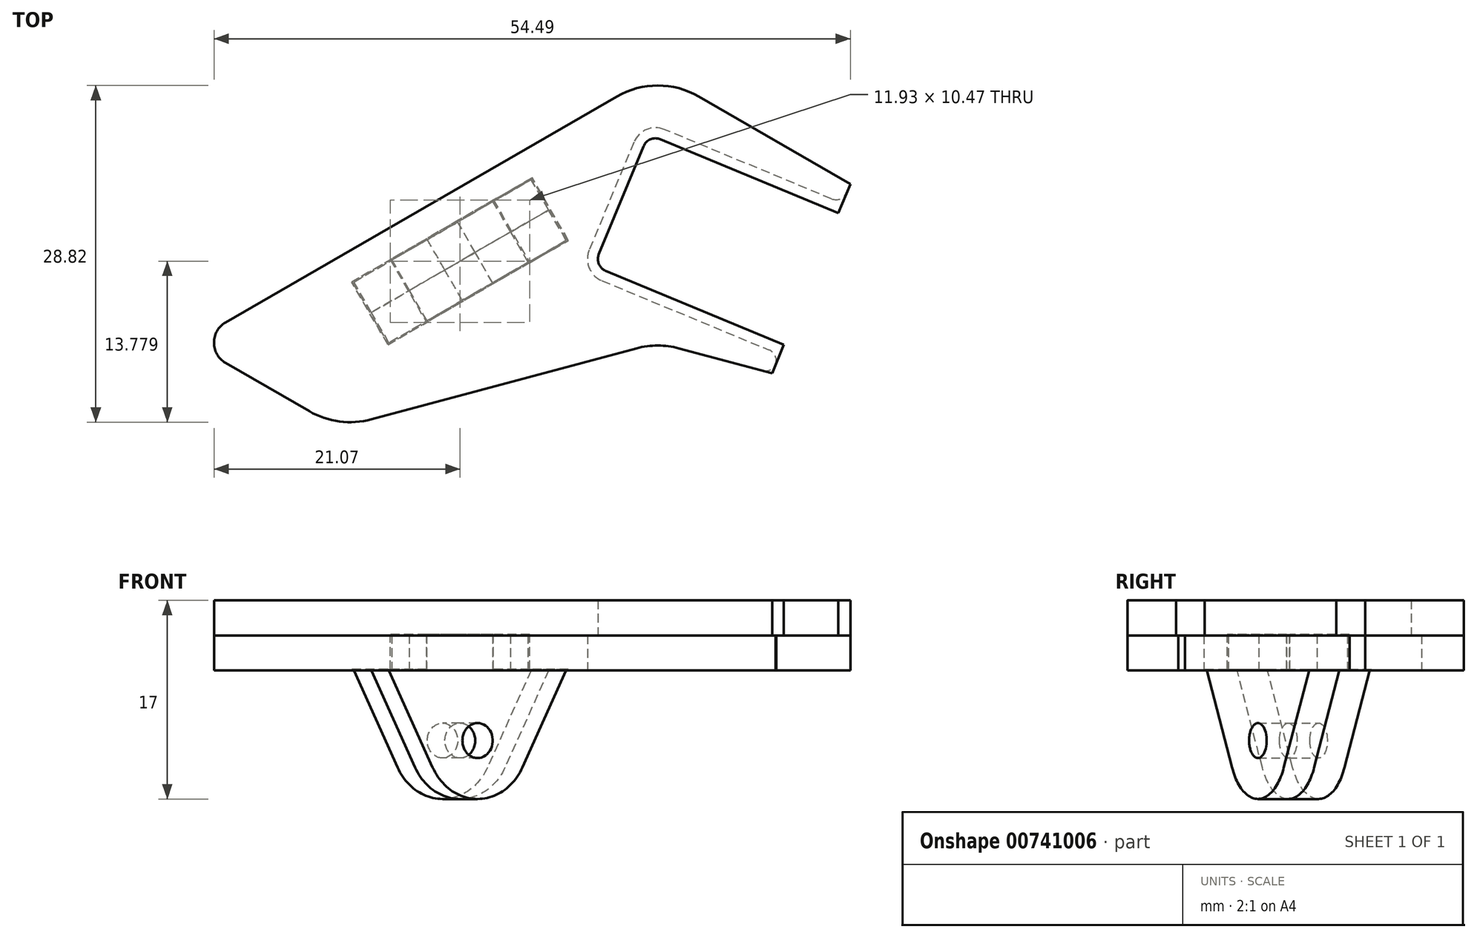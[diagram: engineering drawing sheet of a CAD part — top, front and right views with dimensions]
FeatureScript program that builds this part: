
annotation { "Feature Type Name" : "Feature", "Feature Type Description" : "" }
export const myFeature = defineFeature(function(context is Context, id is Id, definition is map)
    precondition{}
    {
        {
            var Q0;
            Q0=qCreatedBy(makeId("Top.planeOp"),FACE);
            var sketch = newSketch(context, id + "F0", { "sketchPlane" : qUnion([Q0])});
            skLineSegment(sketch, "E0", {"start": v(-37, 1.73) * mm, "end": v(-3.5, 21.07) * mm});
            skLineSegment(sketch, "E1", {"start": v(40, 0) * mm, "end": v(21.73, 10.55) * mm, "construction": true});
            skLineSegment(sketch, "E2", {"start": v(-1.81, -0.49) * mm, "end": v(-24.52, -6.57) * mm});
            skLineSegment(sketch, "E3", {"start": v(0, 0) * mm, "end": v(0, 23.1) * mm, "construction": true});
            skLineSegment(sketch, "E4", {"start": v(40, 0) * mm, "end": v(27.32, -7.32) * mm, "construction": true});
            skLineSegment(sketch, "E5", {"start": v(-29.83, -5.87) * mm, "end": v(-40, 0) * mm});
            skLineSegment(sketch, "E6", {"start": v(27.32, -7.32) * mm, "end": v(0, -23.1) * mm, "construction": true});
            skLineSegment(sketch, "E7", {"start": v(0, -23.1) * mm, "end": v(-37, -1.73) * mm, "construction": true});
            skLineSegment(sketch, "E8", {"start": v(13.99, -0.3) * mm, "end": v(17.82, 8.93) * mm});
            skLineSegment(sketch, "E9", {"start": v(16.73, 11.54) * mm, "end": v(0.57, 18.24) * mm});
            skLineSegment(sketch, "E10", {"start": v(-2.05, 17.16) * mm, "end": v(-5.87, 7.92) * mm});
            skLineSegment(sketch, "E11", {"start": v(-4.8, 5.3) * mm, "end": v(11.38, -1.4) * mm});
            skPoint(sketch, "E12.visualSharp", {"position": v(-6.64, 6.07) * mm});
            skArc(sketch, "E12.filletArc", {"start": v(-5.87, 7.92) * mm, "mid": v(-5.87, 6.39) * mm, "end": v(-4.8, 5.3) * mm});
            skPoint(sketch, "E13.visualSharp", {"position": v(-1.28, 19) * mm});
            skArc(sketch, "E13.filletArc", {"start": v(0.57, 18.24) * mm, "mid": v(-0.96, 18.24) * mm, "end": v(-2.05, 17.16) * mm});
            skPoint(sketch, "E14.visualSharp", {"position": v(18.58, 10.78) * mm});
            skArc(sketch, "E14.filletArc", {"start": v(17.82, 8.93) * mm, "mid": v(17.82, 10.46) * mm, "end": v(16.73, 11.54) * mm});
            skPoint(sketch, "E15.visualSharp", {"position": v(13.22, -2.16) * mm});
            skArc(sketch, "E15.filletArc", {"start": v(11.38, -1.4) * mm, "mid": v(12.9, -1.4) * mm, "end": v(13.99, -0.3) * mm});
            skLineSegment(sketch, "E16", {"start": v(16.64, -1.76) * mm, "end": v(20.73, 8.12) * mm});
            skLineSegment(sketch, "E17", {"start": v(15.63, -4.19) * mm, "end": v(27.32, -7.32) * mm, "construction": true});
            skLineSegment(sketch, "E18", {"start": v(13.09, -3.5) * mm, "end": v(1.81, -0.49) * mm});
            skLineSegment(sketch, "E19", {"start": v(3.5, 21.07) * mm, "end": v(19.45, 11.86) * mm});
            skPoint(sketch, "E20.visualSharp", {"position": v(15.63, -4.19) * mm});
            skArc(sketch, "E20.filletArc", {"start": v(13.09, -3.5) * mm, "mid": v(15.2, -3.3) * mm, "end": v(16.64, -1.76) * mm});
            skPoint(sketch, "E21.visualSharp", {"position": v(21.73, 10.55) * mm});
            skArc(sketch, "E21.filletArc", {"start": v(20.73, 8.12) * mm, "mid": v(20.8, 10.23) * mm, "end": v(19.45, 11.86) * mm});
            skPoint(sketch, "E22.visualSharp", {"position": v(0, 0) * mm});
            skArc(sketch, "E22.filletArc", {"start": v(1.81, -0.49) * mm, "mid": v(0, -0.25) * mm, "end": v(-1.81, -0.49) * mm});
            skPoint(sketch, "E23.visualSharp", {"position": v(-27.32, -7.32) * mm});
            skArc(sketch, "E23.filletArc", {"start": v(-29.83, -5.87) * mm, "mid": v(-27.25, -6.75) * mm, "end": v(-24.52, -6.57) * mm});
            skPoint(sketch, "E24.visualSharp", {"position": v(0, 23.1) * mm});
            skArc(sketch, "E24.filletArc", {"start": v(3.5, 21.07) * mm, "mid": v(0, 22.01) * mm, "end": v(-3.5, 21.07) * mm});
            skPoint(sketch, "E25.visualSharp", {"position": v(-40, 0) * mm});
            skArc(sketch, "E25.filletArc", {"start": v(-37, 1.73) * mm, "mid": v(-38, 0) * mm, "end": v(-37, -1.73) * mm});
            skSolve(sketch);
        }
        {
            var Q0;
            Q0=makeQuery(id+"F0.imprint","IMPRINT",FACE,{"disambiguationData":[TD([[makeQuery(id+"F0.imprint","IMPRINT",EDGE,{"derivedFrom":sQuery(id+"F0.wireOp",EDGE,"E0")}),-1.0]])]});
            extrude(context, id + "F1", {"entities" : qUnion([Q0]), "depth" : 3 * mm, "offsetDistance" : 25 * mm});
        }
        {
            var Q0;
            Q0=makeQuery(id+"F1.opExtrude","CAP_FACE",FACE,{"disambiguationData":[OSD([sQuery(id+"F0.wireOp",EDGE,"E0"),sQuery(id+"F0.wireOp",EDGE,"E2"),sQuery(id+"F0.wireOp",EDGE,"E5"),sQuery(id+"F0.wireOp",EDGE,"E8"),sQuery(id+"F0.wireOp",EDGE,"E9"),sQuery(id+"F0.wireOp",EDGE,"E10"),sQuery(id+"F0.wireOp",EDGE,"E11"),sQuery(id+"F0.wireOp",EDGE,"E12.filletArc"),sQuery(id+"F0.wireOp",EDGE,"E13.filletArc"),sQuery(id+"F0.wireOp",EDGE,"E14.filletArc"),sQuery(id+"F0.wireOp",EDGE,"E15.filletArc"),sQuery(id+"F0.wireOp",EDGE,"E16"),sQuery(id+"F0.wireOp",EDGE,"E18"),sQuery(id+"F0.wireOp",EDGE,"E19"),sQuery(id+"F0.wireOp",EDGE,"E20.filletArc"),sQuery(id+"F0.wireOp",EDGE,"E21.filletArc"),sQuery(id+"F0.wireOp",EDGE,"E22.filletArc"),sQuery(id+"F0.wireOp",EDGE,"E23.filletArc"),sQuery(id+"F0.wireOp",EDGE,"E24.filletArc"),sQuery(id+"F0.wireOp",EDGE,"E25.filletArc")])],"isStart":false});
            var sketch = newSketch(context, id + "F2", { "sketchPlane" : qUnion([Q0])});
            skArc(sketch, "E26.0", {"start": v(-5.04, 7.58) * mm, "mid": v(-5.04, 6.73) * mm, "end": v(-4.45, 6.14) * mm});
            skLineSegment(sketch, "E26.1", {"start": v(-1.22, 16.81) * mm, "end": v(-5.04, 7.58) * mm});
            skLineSegment(sketch, "E26.2", {"start": v(-4.45, 6.14) * mm, "end": v(11.72, -0.56) * mm});
            skArc(sketch, "E26.3", {"start": v(0.22, 17.4) * mm, "mid": v(-0.62, 17.4) * mm, "end": v(-1.22, 16.81) * mm});
            skArc(sketch, "E26.4", {"start": v(11.72, -0.56) * mm, "mid": v(12.56, -0.56) * mm, "end": v(13.16, 0.04) * mm});
            skLineSegment(sketch, "E26.5", {"start": v(13.16, 0.04) * mm, "end": v(16.98, 9.28) * mm});
            skArc(sketch, "E26.6", {"start": v(16.98, 9.28) * mm, "mid": v(16.98, 10.12) * mm, "end": v(16.39, 10.71) * mm});
            skLineSegment(sketch, "E26.7", {"start": v(16.39, 10.71) * mm, "end": v(0.22, 17.4) * mm});
            skLineSegment(sketch, "E27.0", {"start": v(13.09, -3.5) * mm, "end": v(1.81, -0.49) * mm});
            skArc(sketch, "E28.0", {"start": v(13.09, -3.5) * mm, "mid": v(15.2, -3.3) * mm, "end": v(16.64, -1.76) * mm});
            skLineSegment(sketch, "E29.0", {"start": v(16.64, -1.76) * mm, "end": v(20.73, 8.12) * mm});
            skArc(sketch, "E30.0", {"start": v(20.73, 8.12) * mm, "mid": v(20.8, 10.23) * mm, "end": v(19.45, 11.86) * mm});
            skLineSegment(sketch, "E31.0", {"start": v(3.5, 21.07) * mm, "end": v(19.45, 11.86) * mm});
            skArc(sketch, "E32.0", {"start": v(3.5, 21.07) * mm, "mid": v(0, 22.01) * mm, "end": v(-3.5, 21.07) * mm});
            skLineSegment(sketch, "E33.0", {"start": v(-37, 1.73) * mm, "end": v(-3.5, 21.07) * mm});
            skArc(sketch, "E34.0", {"start": v(-37, 1.73) * mm, "mid": v(-38, 0) * mm, "end": v(-37, -1.73) * mm});
            skLineSegment(sketch, "E35.0", {"start": v(-29.83, -5.87) * mm, "end": v(-37, -1.73) * mm});
            skArc(sketch, "E36.0", {"start": v(-29.83, -5.87) * mm, "mid": v(-27.25, -6.75) * mm, "end": v(-24.52, -6.57) * mm});
            skLineSegment(sketch, "E37.0", {"start": v(-1.81, -0.49) * mm, "end": v(-24.52, -6.57) * mm});
            skArc(sketch, "E38.0", {"start": v(1.81, -0.49) * mm, "mid": v(0, -0.25) * mm, "end": v(-1.81, -0.49) * mm});
            skSolve(sketch);
        }
        {
            var Q0;
            Q0=qSketchRegion(id+"F2",true);
            extrude(context, id + "F3", {"entities" : qUnion([Q0]), "depth" : 3 * mm, "offsetDistance" : 25 * mm});
        }
        {
            var Q0;
            Q0=makeQuery(id+"F1.opExtrude","CAP_FACE",FACE,{"disambiguationData":[OSD([sQuery(id+"F0.wireOp",EDGE,"E0"),sQuery(id+"F0.wireOp",EDGE,"E2"),sQuery(id+"F0.wireOp",EDGE,"E5"),sQuery(id+"F0.wireOp",EDGE,"E8"),sQuery(id+"F0.wireOp",EDGE,"E9"),sQuery(id+"F0.wireOp",EDGE,"E10"),sQuery(id+"F0.wireOp",EDGE,"E11"),sQuery(id+"F0.wireOp",EDGE,"E12.filletArc"),sQuery(id+"F0.wireOp",EDGE,"E13.filletArc"),sQuery(id+"F0.wireOp",EDGE,"E14.filletArc"),sQuery(id+"F0.wireOp",EDGE,"E15.filletArc"),sQuery(id+"F0.wireOp",EDGE,"E16"),sQuery(id+"F0.wireOp",EDGE,"E18"),sQuery(id+"F0.wireOp",EDGE,"E19"),sQuery(id+"F0.wireOp",EDGE,"E20.filletArc"),sQuery(id+"F0.wireOp",EDGE,"E21.filletArc"),sQuery(id+"F0.wireOp",EDGE,"E22.filletArc"),sQuery(id+"F0.wireOp",EDGE,"E23.filletArc"),sQuery(id+"F0.wireOp",EDGE,"E24.filletArc"),sQuery(id+"F0.wireOp",EDGE,"E25.filletArc")])],"isStart":true});
            var sketch = newSketch(context, id + "F4", { "sketchPlane" : qUnion([Q0])});
            skLineSegment(sketch, "E39.0", {"start": v(-29.83, 5.87) * mm, "end": v(-37, 1.73) * mm});
            skArc(sketch, "E40.0", {"start": v(-29.83, 5.87) * mm, "mid": v(-27.25, 6.75) * mm, "end": v(-24.52, 6.57) * mm});
            skArc(sketch, "E41.0", {"start": v(-37, -1.73) * mm, "mid": v(-38, 0) * mm, "end": v(-37, 1.73) * mm});
            skLineSegment(sketch, "E42.0", {"start": v(-1.81, 0.49) * mm, "end": v(-24.52, 6.57) * mm});
            skLineSegment(sketch, "E43.0", {"start": v(-37, -1.73) * mm, "end": v(-24.97, -8.68) * mm});
            skLineSegment(sketch, "E44", {"start": v(-24.97, -8.68) * mm, "end": v(-17.31, -2.25) * mm});
            skLineSegment(sketch, "E45", {"start": v(-17.31, -2.25) * mm, "end": v(-1.81, 0.49) * mm});
            skPoint(sketch, "E46.orphan", {"position": v(-3.5, -21.07) * mm});
            skSolve(sketch);
        }
        {
            var Q0;
            Q0=makeQuery(id+"F1.opExtrude","SWEPT_FACE",FACE,{"disambiguationData":[OSD([sQuery(id+"F0.wireOp",EDGE,"E0")])]});
            cPlane(context, id + "F5", {"entities" : qUnion([Q0]), "cplaneType" : CPlaneType.OFFSET, "offset" : 2.5 * mm, "oppositeDirection" : true, "width" : 150 * mm, "height" : 150 * mm});
        }
        {
            var Q0;
            Q0=qCreatedBy(id+"F5.planeOp",FACE);
            var sketch = newSketch(context, id + "F6", { "sketchPlane" : qUnion([Q0])});
            skCircle(sketch, "E47", {"center": v(11.18, -6) * mm, "radius": 1.5 * mm});
            skCircle(sketch, "E48", {"center": v(11.18, -6) * mm, "radius": 5 * mm});
            skLineSegment(sketch, "E49", {"start": v(15.61, -8.3) * mm, "end": v(19.94, 0) * mm});
            skLineSegment(sketch, "E50", {"start": v(19.94, 0) * mm, "end": v(2.42, 0) * mm});
            skLineSegment(sketch, "E51", {"start": v(2.42, 0) * mm, "end": v(6.74, -8.3) * mm});
            skLineSegment(sketch, "E52.bottom", {"start": v(6.18, 0) * mm, "end": v(16.18, 0) * mm});
            skLineSegment(sketch, "E52.top", {"start": v(6.18, 3) * mm, "end": v(16.18, 3) * mm});
            skLineSegment(sketch, "E52.left", {"start": v(6.18, 0) * mm, "end": v(6.18, 3) * mm});
            skLineSegment(sketch, "E52.right", {"start": v(16.18, 0) * mm, "end": v(16.18, 3) * mm});
            skPoint(sketch, "E52.middle", {"position": v(11.18, 1.5) * mm});
            skPoint(sketch, "E52.middle.positionSnap0", {"position": v(11.18, 0) * mm});
            skPoint(sketch, "E52.centerSnap0", {"position": v(11.18, 0) * mm});
            skSolve(sketch);
        }
        {
            var Q0;
            Q0=qSketchRegion(id+"F6",true);
            extrude(context, id + "F7", {"entities" : qUnion([Q0]), "oppositeDirection" : true, "depth" : 3 * mm, "offsetDistance" : 25 * mm});
        }
        {
            var Q0;
            Q0=makeQuery(id+"F7.opExtrude","SWEPT_BODY",BODY,{"disambiguationData":[OSD([sQuery(id+"F6.wireOp",EDGE,"E47"),sQuery(id+"F6.wireOp",EDGE,"E48"),sQuery(id+"F6.wireOp",EDGE,"E49"),sQuery(id+"F6.wireOp",EDGE,"E50"),sQuery(id+"F6.wireOp",EDGE,"E51"),sQuery(id+"F6.wireOp",EDGE,"E52.top"),sQuery(id+"F6.wireOp",EDGE,"E52.left"),sQuery(id+"F6.wireOp",EDGE,"E52.right")])]});
            var Q1;
            Q1=makeQuery(id+"F7.opExtrude","SWEPT_EDGE",EDGE,{"disambiguationData":[OSD([sQuery(id+"F6.wireOp",EDGE,"E48"),sQuery(id+"F6.wireOp",EDGE,"E51")])]});
            transform(context, id + "F8", {"entities" : qUnion([Q0]), "transformType" : TransformType.TRANSLATION_ENTITY, "oppositeDirectionEntity" : true, "transformLine" : qUnion([Q1]), "makeCopy" : true});
        }
        {
            var Q0;
            Q0=makeQuery(id+"F8.opPattern","COPY",BODY,{"derivedFrom":makeQuery(id+"F7.opExtrude","SWEPT_BODY",BODY,{"disambiguationData":[OSD([sQuery(id+"F6.wireOp",EDGE,"E47"),sQuery(id+"F6.wireOp",EDGE,"E48"),sQuery(id+"F6.wireOp",EDGE,"E49"),sQuery(id+"F6.wireOp",EDGE,"E50"),sQuery(id+"F6.wireOp",EDGE,"E51"),sQuery(id+"F6.wireOp",EDGE,"E52.top"),sQuery(id+"F6.wireOp",EDGE,"E52.left"),sQuery(id+"F6.wireOp",EDGE,"E52.right")])]}),"instanceName":"1"});
            var Q1;
            Q1=makeQuery(id+"F7.opExtrude","SWEPT_BODY",BODY,{"disambiguationData":[OSD([sQuery(id+"F6.wireOp",EDGE,"E47"),sQuery(id+"F6.wireOp",EDGE,"E48"),sQuery(id+"F6.wireOp",EDGE,"E49"),sQuery(id+"F6.wireOp",EDGE,"E50"),sQuery(id+"F6.wireOp",EDGE,"E51"),sQuery(id+"F6.wireOp",EDGE,"E52.top"),sQuery(id+"F6.wireOp",EDGE,"E52.left"),sQuery(id+"F6.wireOp",EDGE,"E52.right")])]});
            var Q2;
            Q2=makeQuery(id+"F1.opExtrude","SWEPT_BODY",BODY,{"disambiguationData":[OSD([sQuery(id+"F0.wireOp",EDGE,"E0"),sQuery(id+"F0.wireOp",EDGE,"E2"),sQuery(id+"F0.wireOp",EDGE,"E5"),sQuery(id+"F0.wireOp",EDGE,"E8"),sQuery(id+"F0.wireOp",EDGE,"E9"),sQuery(id+"F0.wireOp",EDGE,"E10"),sQuery(id+"F0.wireOp",EDGE,"E11"),sQuery(id+"F0.wireOp",EDGE,"E12.filletArc"),sQuery(id+"F0.wireOp",EDGE,"E13.filletArc"),sQuery(id+"F0.wireOp",EDGE,"E14.filletArc"),sQuery(id+"F0.wireOp",EDGE,"E15.filletArc"),sQuery(id+"F0.wireOp",EDGE,"E16"),sQuery(id+"F0.wireOp",EDGE,"E18"),sQuery(id+"F0.wireOp",EDGE,"E19"),sQuery(id+"F0.wireOp",EDGE,"E20.filletArc"),sQuery(id+"F0.wireOp",EDGE,"E21.filletArc"),sQuery(id+"F0.wireOp",EDGE,"E22.filletArc"),sQuery(id+"F0.wireOp",EDGE,"E23.filletArc"),sQuery(id+"F0.wireOp",EDGE,"E24.filletArc"),sQuery(id+"F0.wireOp",EDGE,"E25.filletArc")])]});
            var Q3;
            Q3=makeQuery(id+"F3.opExtrude","SWEPT_BODY",BODY,{"disambiguationData":[OSD([sQuery(id+"F2.wireOp",EDGE,"E26.0"),sQuery(id+"F2.wireOp",EDGE,"E26.1"),sQuery(id+"F2.wireOp",EDGE,"E26.2"),sQuery(id+"F2.wireOp",EDGE,"E26.3"),sQuery(id+"F2.wireOp",EDGE,"E26.4"),sQuery(id+"F2.wireOp",EDGE,"E26.5"),sQuery(id+"F2.wireOp",EDGE,"E26.6"),sQuery(id+"F2.wireOp",EDGE,"E26.7"),sQuery(id+"F2.wireOp",EDGE,"E27.0"),sQuery(id+"F2.wireOp",EDGE,"E28.0"),sQuery(id+"F2.wireOp",EDGE,"E29.0"),sQuery(id+"F2.wireOp",EDGE,"E30.0"),sQuery(id+"F2.wireOp",EDGE,"E31.0"),sQuery(id+"F2.wireOp",EDGE,"E32.0"),sQuery(id+"F2.wireOp",EDGE,"E33.0"),sQuery(id+"F2.wireOp",EDGE,"E34.0"),sQuery(id+"F2.wireOp",EDGE,"E35.0"),sQuery(id+"F2.wireOp",EDGE,"E36.0"),sQuery(id+"F2.wireOp",EDGE,"E37.0"),sQuery(id+"F2.wireOp",EDGE,"E38.0")])]});
            booleanBodies(context, id + "F9", {"operationType" : BooleanOperationType.SUBTRACTION, "tools" : qUnion([Q0, Q1]), "targets" : qUnion([Q2, Q3]), "offset" : true, "offsetAll" : true, "offsetDistance" : .1 * mm, "keepTools" : true});
        }
        {
            var Q0;
            Q0=makeQuery(id+"F1.opExtrude","CAP_FACE",FACE,{"disambiguationData":[OSD([sQuery(id+"F0.wireOp",EDGE,"E0"),sQuery(id+"F0.wireOp",EDGE,"E2"),sQuery(id+"F0.wireOp",EDGE,"E5"),sQuery(id+"F0.wireOp",EDGE,"E8"),sQuery(id+"F0.wireOp",EDGE,"E9"),sQuery(id+"F0.wireOp",EDGE,"E10"),sQuery(id+"F0.wireOp",EDGE,"E11"),sQuery(id+"F0.wireOp",EDGE,"E12.filletArc"),sQuery(id+"F0.wireOp",EDGE,"E13.filletArc"),sQuery(id+"F0.wireOp",EDGE,"E14.filletArc"),sQuery(id+"F0.wireOp",EDGE,"E15.filletArc"),sQuery(id+"F0.wireOp",EDGE,"E16"),sQuery(id+"F0.wireOp",EDGE,"E18"),sQuery(id+"F0.wireOp",EDGE,"E19"),sQuery(id+"F0.wireOp",EDGE,"E20.filletArc"),sQuery(id+"F0.wireOp",EDGE,"E21.filletArc"),sQuery(id+"F0.wireOp",EDGE,"E22.filletArc"),sQuery(id+"F0.wireOp",EDGE,"E23.filletArc"),sQuery(id+"F0.wireOp",EDGE,"E24.filletArc"),sQuery(id+"F0.wireOp",EDGE,"E25.filletArc")])],"isStart":true});
            var sketch = newSketch(context, id + "F10", { "sketchPlane" : qUnion([Q0])});
            skLineSegment(sketch, "E53", {"start": v(10.45, 1) * mm, "end": v(8.09, 6.72) * mm});
            skLineSegment(sketch, "E54", {"start": v(16.5, -13.57) * mm, "end": v(10.45, 1) * mm});
            skLineSegment(sketch, "E55", {"start": v(8.09, 6.72) * mm, "end": v(14.2, 9.26) * mm});
            skLineSegment(sketch, "E56", {"start": v(14.2, 9.26) * mm, "end": v(23.7, -13.64) * mm});
            skLineSegment(sketch, "E57", {"start": v(23.7, -13.64) * mm, "end": v(16.5, -13.57) * mm});
            skSolve(sketch);
        }
        {
            var Q0;
            Q0 = qSketchRegion(id + "F10", true);
            extrude(context, id + "F11", {"entities" : qUnion([Q0]), "operationType" : NewBodyOperationType.REMOVE, "oppositeDirection" : true, "depth" : 25 * mm, "offsetDistance" : 25 * mm});
        }
        {
            var Q0;
            Q0=makeQuery(id+"F11.boolean.opBoolean","INTERSECT",EDGE,{"derivedFrom":[makeQuery(id+"F1.opExtrude","SWEPT_FACE",FACE,{"disambiguationData":[OSD([sQuery(id+"F0.wireOp",EDGE,"E18")])]}),makeQuery(id+"F11.opExtrude","SWEPT_FACE",FACE,{"disambiguationData":[OSD([sQuery(id+"F10.wireOp",EDGE,"E53"),sQuery(id+"F10.wireOp",EDGE,"E54")])]})]});
            var Q1;
            Q1=makeQuery(id+"F11.boolean.opBoolean","INTERSECT",EDGE,{"derivedFrom":[makeQuery(id+"F1.opExtrude","SWEPT_FACE",FACE,{"disambiguationData":[OSD([sQuery(id+"F0.wireOp",EDGE,"E11")])]}),makeQuery(id+"F11.opExtrude","SWEPT_FACE",FACE,{"disambiguationData":[OSD([sQuery(id+"F10.wireOp",EDGE,"E53"),sQuery(id+"F10.wireOp",EDGE,"E54")])]})]});
            var Q2;
            Q2=makeQuery(id+"F11.boolean.opBoolean","INTERSECT",EDGE,{"derivedFrom":[makeQuery(id+"F1.opExtrude","SWEPT_FACE",FACE,{"disambiguationData":[OSD([sQuery(id+"F0.wireOp",EDGE,"E9")])]}),makeQuery(id+"F11.opExtrude","SWEPT_FACE",FACE,{"disambiguationData":[OSD([sQuery(id+"F10.wireOp",EDGE,"E53"),sQuery(id+"F10.wireOp",EDGE,"E54")])]})]});
            var Q3;
            Q3=makeQuery(id+"F11.boolean.opBoolean","COPY",EDGE,{"derivedFrom":makeQuery(id+"F11.opExtrude","SWEPT_EDGE",EDGE,{"disambiguationData":[OSD([sQuery(id+"F0.wireOp",EDGE,"E19"),sQuery(id+"F10.wireOp",EDGE,"E54"),sQuery(id+"F10.wireOp",EDGE,"E57")])]})});
            fillet(context, id + "F12", {"entities" : qUnion([Q0, Q1, Q2, Q3]), "radius" : 1 * mm, "tangentPropagation" : true, "allowEdgeOverflow" : false});
        }
    });
